# Revit family: ESFR-25-TY9229_Imperial
name_source: partatom
category: Sprinklers
units: mm (PartAtom-declared; Revit-internal decimal feet)

## family parameters
Always vertical = Yes
Cut with Voids When Loaded = No
Maintain Annotation Orientation = No
Part Type = Normal
Room Calculation Point = No
Round Connector Dimension = Use Diameter
Shared = No
Work Plane-Based = No

## types (12) — shared parameters
COBie = Yes
COBie.Component.Name = Sprinklers:Dry Pendent
COBie.Type = Yes
COBie.Type.AssetType = Fixed
COBie.Type.Category = Pr_70_55_97_84:Sprinklers
COBie.Type.DurationUnit = year
COBie.Type.Manufacturer = Tyco Fire Protection Products
COBie.Type.Material = Natural Brass
COBie.Type.NominalHeight = 0' - 0"
COBie.Type.NominalLength = 0' - 0"
COBie.Type.NominalWidth = 0' - 0"
COBie.Type.Shape = Cylinder
COBie.Type.WarrantyGuarantorParts = http://tycofsbp.com
TFPPTerms_of_Sale.pdf
Coverage = Standard
Coverage_ = Standard
Default Elevation = 0' - 0"
Finish_ = Natural Brass
K-Factor = 25.2
Manufacturer = Tyco Fire Protection Products
Manufacturer URL = www.tyco-fire.com
Material_ = Galvanized Steel
Model = ESFR-25
Orifice = Extra Large
Orifice Size = 1"
Outside Diameter 1 = 2"
Response = Quick
Response_ = Quick
SIN No = TY9229
Technical Data Sheet No = TFP329
zero-valued in all types: COBie.Type.ReplacementCost, Style Id

## per-type parameters (varying)
| type | COBie.Component.Description | COBie.Type.ModelNumber | COBie.Type.ModelReference | COBie.Type.Size | Description | ND Integer 1 | ND Lookup 1 | Nominal Diameter 1 | Part No | Takeout 1 | Temperature Rating |
| Tyco_ESFR-25_Dry Pendent_165°F/74°C_1-1/4"_Natural Brass_61-541-1-230 | ESFR-25 Dry Pendent ESFR 165°F K25.2 1-1/4 ISO | 61-541-1-230 | ESFR-25 Dry Pendent ESFR 165°F K25.2 1-1/4 ISO | 1-1/4"(DN32) | ESFR-25 Dry Pendent Brass 165°F/74°C 25.2K 1-1/4" Grooved/ISO 23" | 20 | 1" | 1" | 61-541-1-230 | 23" | 165 °F |
| Tyco_ESFR-25_Dry Pendent_165°F/74°C_1-1/4"_Natural Brass_61-541-1-300 | ESFR-25 Dry Pendent ESFR 165°F K25.2 1-1/4 ISO | 61-541-1-300 | ESFR-25 Dry Pendent ESFR 165°F K25.2 1-1/4 ISO | 1-1/4"(DN32) | ESFR-25 Dry Pendent Brass 165°F/74°C 25.2K 1-1/4" Grooved/ISO 30" | 20 | 1" | 1" | 61-541-1-300 | 30" | 165 °F |
| Tyco_ESFR-25_Dry Pendent_165°F/74°C_1-1/4"_Natural Brass_61-541-1-360 | ESFR-25 Dry Pendent ESFR 165°F K25.2 1-1/4 ISO | 61-541-1-360 | ESFR-25 Dry Pendent ESFR 165°F K25.2 1-1/4 ISO | 1-1/4"(DN32) | ESFR-25 Dry Pendent Brass 165°F/74°C 25.2K 1-1/4" Grooved/ISO 36" | 20 | 1" | 1" | 61-541-1-360 | 36" | 165 °F |
| Tyco_ESFR-25_Dry Pendent_212°F/100°C_1-1/4"_Natural Brass_61-542-1-230 | ESFR-25 Dry Pendent ESFR 212°F K25.2 1-1/4 ISO | 61-542-1-230 | ESFR-25 Dry Pendent ESFR 212°F K25.2 1-1/4 ISO | 1-1/4"(DN32) | ESFR-25 Dry Pendent Brass 212°F/100°C 25.2K 1-1/4" Grooved/ISO 23" | 20 | 1" | 1" | 61-542-1-230 | 23" | 212 °F |
| Tyco_ESFR-25_Dry Pendent_212°F/100°C_1-1/4"_Natural Brass_61-542-1-300 | ESFR-25 Dry Pendent ESFR 212°F K25.2 1-1/4 ISO | 61-542-1-300 | ESFR-25 Dry Pendent ESFR 212°F K25.2 1-1/4 ISO | 1-1/4"(DN32) | ESFR-25 Dry Pendent Brass 212°F/100°C 25.2K 1-1/4" Grooved/ISO 30" | 20 | 1" | 1" | 61-542-1-300 | 30" | 212 °F |
| Tyco_ESFR-25_Dry Pendent_212°F/100°C_1-1/4"_Natural Brass_61-542-1-360 | ESFR-25 Dry Pendent ESFR 212°F K25.2 1-1/4 ISO | 61-542-1-320 | ESFR-17 Dry Pendent ESFR 212°F K25.2 1-1/4 ISO | 1-1/4"(DN32) | ESFR-25 Dry Pendent Brass 212°F/100°C 25.2K 1-1/4" Grooved/ISO 36" | 20 | 1" | 1" | 61-542-1-320 | 36" | 212 °F |
| Tyco_ESFR-25_Dry Pendent_165°F/74°C_2"_Natural Brass_61-541-1-230_Grooved | ESFR-25 Dry Pendent ESFR 165°F K25.2 1-1/4 ISO | 61-541-1-230 | ESFR-25 Dry Pendent ESFR 165°F K25.2 1-1/4 ISO | 2"(DN50) | ESFR-25 Dry Pendent Brass 165°F/74°C 25.2K 2" Grooved/ISO 23" | 32 | 2" | 2" | 61-541-1-230 | 23" | 165 °F |
| Tyco_ESFR-25_Dry Pendent_165°F/74°C_2"_Natural Brass_61-541-1-300_Grooved | ESFR-25 Dry Pendent ESFR 165°F K25.2 1-1/4 ISO | 61-541-1-300 | ESFR-17 Dry Pendent ESFR 165°F K25.2 1-1/4 ISO | 2"(DN50) | ESFR-25 Dry Pendent Brass 165°F/74°C 25.2K 2" Grooved/ISO 30" | 32 | 2" | 2" | 61-541-1-300 | 30" | 165 °F |
| Tyco_ESFR-25_Dry Pendent_165°F/74°C_2"_Natural Brass_61-541-1-360_Grooved | ESFR-25 Dry Pendent ESFR 165°F K25.2 1-1/4 ISO | 61-541-1-360 | ESFR-25 Dry Pendent ESFR 165°F K25.2 1-1/4 ISO | 2"(DN50) | ESFR-25 Dry Pendent Brass 165°F/74°C 25.2K 2" Grooved/ISO 36" | 32 | 2" | 2" | 61-541-1-360 | 36" | 165 °F |
| Tyco_ESFR-25_Dry Pendent_212°F/100°C_2"_Natural Brass_61-542-1-230_Grooved | ESFR-25 Dry Pendent ESFR 212°F K25.2 1-1/4 ISO | 61-542-1-230 | ESFR-25 Dry Pendent ESFR 212°F K25.2 1-1/4 ISO | 2"(DN50) | ESFR-25 Dry Pendent Brass 212°F/100°C 25.2K 2" Grooved/ISO 23" | 32 | 2" | 2" | 61-542-1-230 | 23" | 212 °F |
| Tyco_ESFR-25_Dry Pendent_212°F/100°C_2"_Natural Brass_61-542-1-300_Grooved | ESFR-25 Dry Pendent ESFR 212°F K25.2 1-1/4 ISO | 61-542-1-300 | ESFR-25 Dry Pendent ESFR 212°F K25.2 1-1/4 ISO | 2"(DN50) | ESFR-25 Dry Pendent Brass 212°F/100°C 25.2K 2" Grooved/ISO 30" | 32 | 2" | 2" | 61-542-1-300 | 30" | 212 °F |
| Tyco_ESFR-25_Dry Pendent_212°F/100°C_2"_Natural Brass_61-542-1-360_Grooved | ESFR-25 Dry Pendent ESFR 212°F K25.2 1-1/4 ISO | 61-542-1-360 | ESFR-25 Dry Pendent ESFR 212°F K25.2 1-1/4 ISO | 2"(DN50) | ESFR-25 Dry Pendent Brass 212°F/100°C 25.2K 2" Grooved/ISO 36" | 32 | 2" | 2" | 61-542-1-360 | 36" | 212 °F |

## geometry (parser evidence)
native form markers: Sweep x62
no freeform markers — native parametric forms only
